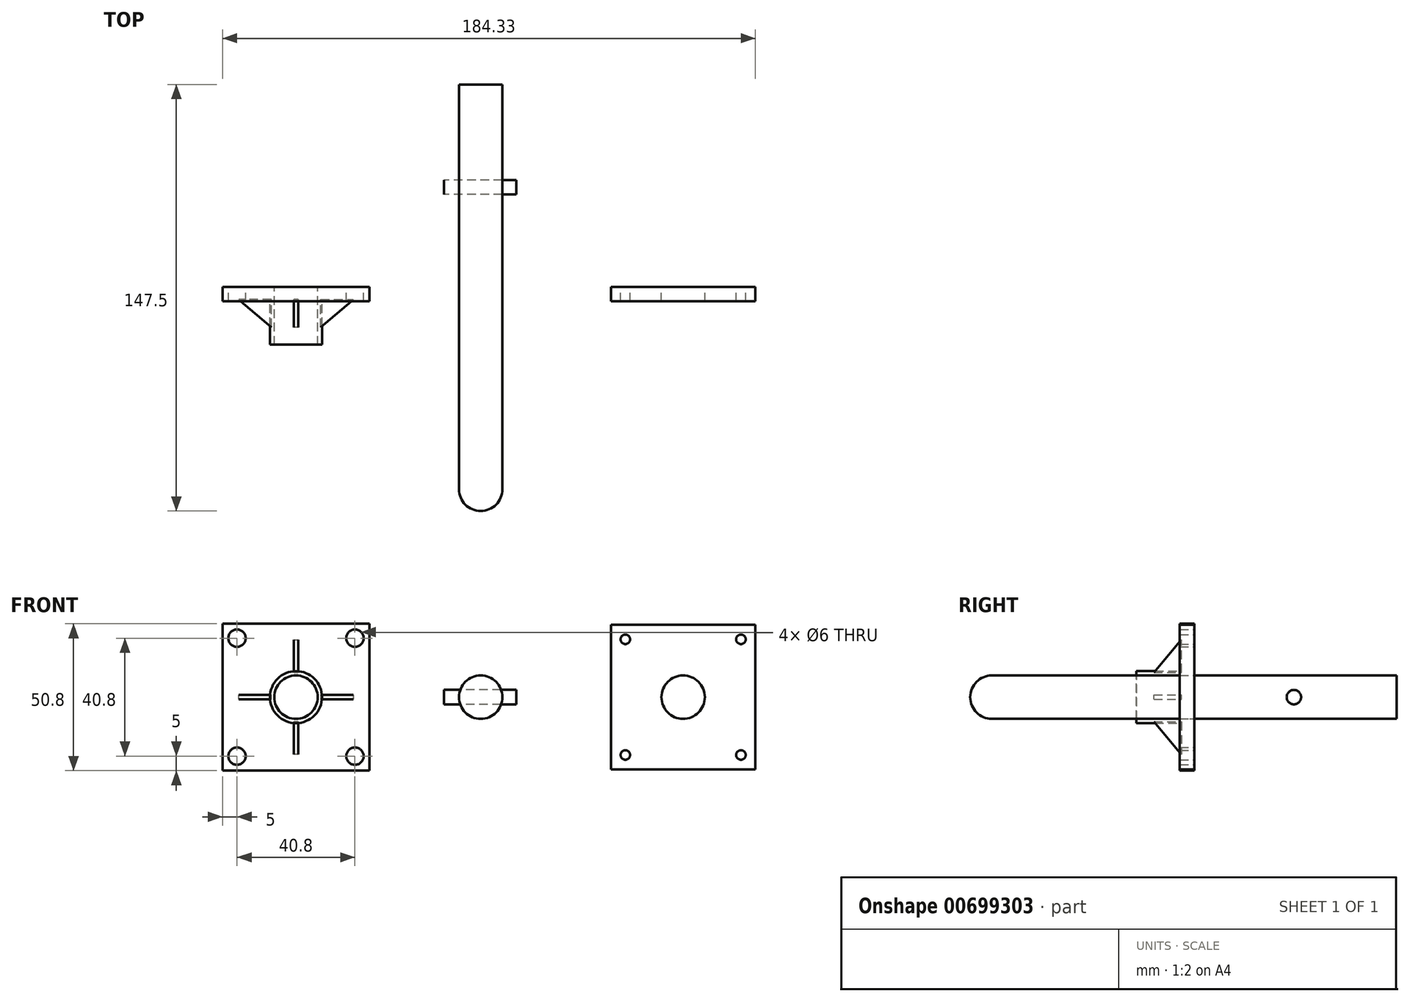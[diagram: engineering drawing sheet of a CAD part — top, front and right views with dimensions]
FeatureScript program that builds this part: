
annotation { "Feature Type Name" : "Feature", "Feature Type Description" : "" }
export const myFeature = defineFeature(function(context is Context, id is Id, definition is map)
    precondition{}
    {
        {
            var Q0;
            Q0=qCreatedBy(makeId("Front.planeOp"),FACE);
            var sketch = newSketch(context, id + "F0", { "sketchPlane" : qUnion([Q0])});
            skLineSegment(sketch, "E0.bottom", {"start": v(-25.4, 25.4) * mm, "end": v(25.4, 25.4) * mm});
            skLineSegment(sketch, "E0.top", {"start": v(-25.4, -25.4) * mm, "end": v(25.4, -25.4) * mm});
            skLineSegment(sketch, "E0.left", {"start": v(-25.4, 25.4) * mm, "end": v(-25.4, -25.4) * mm});
            skLineSegment(sketch, "E0.right", {"start": v(25.4, 25.4) * mm, "end": v(25.4, -25.4) * mm});
            skLineSegment(sketch, "E1", {"start": v(-20.4, 20.4) * mm, "end": v(-20.4, -20.4) * mm, "construction": true});
            skLineSegment(sketch, "E2", {"start": v(22.07, 20.4) * mm, "end": v(-16.45, 20.4) * mm, "construction": true});
            skCircle(sketch, "E3", {"center": v(-20.4, 20.4) * mm, "radius": 3 * mm});
            skLineSegment(sketch, "E4", {"start": v(-20.4, -20.4) * mm, "end": v(20.4, -20.4) * mm, "construction": true});
            skCircle(sketch, "E5", {"center": v(-20.4, -20.4) * mm, "radius": 3 * mm});
            skLineSegment(sketch, "E6", {"start": v(20.4, -20.4) * mm, "end": v(20.4, 20.4) * mm, "construction": true});
            skCircle(sketch, "E7", {"center": v(20.4, 20.4) * mm, "radius": 3 * mm});
            skCircle(sketch, "E8", {"center": v(20.4, -20.4) * mm, "radius": 3 * mm});
            skLineSegment(sketch, "E9", {"start": v(0, 25.4) * mm, "end": v(0, -20.4) * mm, "construction": true});
            skLineSegment(sketch, "E10", {"start": v(-20.4, 0) * mm, "end": v(20.4, 0) * mm, "construction": true});
            skCircle(sketch, "E11", {"center": v(0, 0) * mm, "radius": 7.5 * mm});
            skSolve(sketch);
        }
        {
            var Q0;
            Q0=makeQuery(id+"F0.imprint","IMPRINT",FACE,{"disambiguationData":[TD([[makeQuery(id+"F0.imprint","IMPRINT",EDGE,{"derivedFrom":sQuery(id+"F0.wireOp",EDGE,"E0.bottom")}),-1.0]])]});
            extrude(context, id + "F1", {"entities" : qUnion([Q0]), "depth" : 5 * mm, "offsetDistance" : 25 * mm});
        }
        {
            var Q0;
            Q0=makeQuery(id+"F1.opExtrude","CAP_FACE",FACE,{"disambiguationData":[OSD([sQuery(id+"F0.wireOp",EDGE,"E0.bottom"),sQuery(id+"F0.wireOp",EDGE,"E0.top"),sQuery(id+"F0.wireOp",EDGE,"E0.left"),sQuery(id+"F0.wireOp",EDGE,"E0.right"),sQuery(id+"F0.wireOp",EDGE,"E3"),sQuery(id+"F0.wireOp",EDGE,"E5"),sQuery(id+"F0.wireOp",EDGE,"E7"),sQuery(id+"F0.wireOp",EDGE,"E8"),sQuery(id+"F0.wireOp",EDGE,"E11")])],"isStart":false});
            var sketch = newSketch(context, id + "F2", { "sketchPlane" : qUnion([Q0])});
            skCircle(sketch, "E12", {"center": v(0, 0) * mm, "radius": 7.5 * mm});
            skCircle(sketch, "E13", {"center": v(0, 0) * mm, "radius": 9 * mm});
            skSolve(sketch);
        }
        {
            var Q0;
            Q0=makeQuery(id+"F2.imprint","IMPRINT",FACE,{"disambiguationData":[TD([[makeQuery(id+"F2.imprint","IMPRINT",EDGE,{"derivedFrom":sQuery(id+"F2.wireOp",EDGE,"E12")}),-1.0]])]});
            extrude(context, id + "F3", {"entities" : qUnion([Q0]), "operationType" : NewBodyOperationType.ADD, "depth" : 15 * mm, "offsetDistance" : 25 * mm});
        }
        {
            var Q0;
            Q0=qCreatedBy(makeId("Top.planeOp"),FACE);
            var sketch = newSketch(context, id + "F4", { "sketchPlane" : qUnion([Q0])});
            skLineSegment(sketch, "E14", {"start": v(8.55, -4.4) * mm, "end": v(19.84, -4.4) * mm});
            skLineSegment(sketch, "E15", {"start": v(19.84, -4.4) * mm, "end": v(8.55, -13.98) * mm});
            skLineSegment(sketch, "E16", {"start": v(8.55, -13.98) * mm, "end": v(8.55, -4.4) * mm});
            skSolve(sketch);
        }
        {
            var Q0;
            Q0=makeQuery(id+"F4.imprint","IMPRINT",FACE,{"disambiguationData":[TD([[makeQuery(id+"F4.imprint","IMPRINT",EDGE,{"derivedFrom":sQuery(id+"F4.wireOp",EDGE,"E14")}),-1.0]])]});
            extrude(context, id + "F5", {"entities" : qUnion([Q0]), "endBound" : BoundingType.SYMMETRIC, "depth" : 1.5 * mm, "offsetDistance" : 25 * mm});
        }
        {
            var Q0;
            Q0=makeQuery(id+"F5.opExtrude","SWEPT_BODY",BODY,{"disambiguationData":[OSD([sQuery(id+"F4.wireOp",EDGE,"E14"),sQuery(id+"F4.wireOp",EDGE,"E15"),sQuery(id+"F4.wireOp",EDGE,"E16")])]});
            var Q1;
            Q1=makeQuery(id+"F3.opExtrude","CAP_EDGE",EDGE,{"disambiguationData":[OSD([sQuery(id+"F2.wireOp",EDGE,"E12")])],"isStart":false});
            circularPattern(context, id + "F6", {"entities" : qUnion([Q0]), "axis" : qUnion([Q1]), "angle" : 360 * degree, "instanceCount" : 4, "equalSpace" : true});
        }
        {
            var Q0;
            Q0=qCreatedBy(makeId("Front.planeOp"),FACE);
            var sketch = newSketch(context, id + "F7", { "sketchPlane" : qUnion([Q0])});
            skCircle(sketch, "E17", {"center": v(63.9, 0) * mm, "radius": 7.5 * mm});
            skLineSegment(sketch, "E18", {"start": v(63.9, 0) * mm, "end": v(56.4, 0) * mm, "construction": true});
            skSolve(sketch);
        }
        {
            var Q0;
            Q0 = qSketchRegion(id + "F7", true);
            extrude(context, id + "F8", {"entities" : qUnion([Q0]), "endBound" : BoundingType.SYMMETRIC, "depth" : 140 * mm, "offsetDistance" : 25 * mm});
        }
        {
            var Q0;
            Q0=makeQuery(id+"F8.opExtrude","CAP_FACE",FACE,{"disambiguationData":[OSD([sQuery(id+"F7.wireOp",EDGE,"E17")])],"isStart":false});
            var sketch = newSketch(context, id + "F9", { "sketchPlane" : qUnion([Q0])});
            skLineSegment(sketch, "E19", {"start": v(44.74, 0) * mm, "end": v(63.9, 0) * mm, "construction": true});
            skArc(sketch, "E20", {"start": v(51.35, 0) * mm, "mid": v(63.9, 12.54) * mm, "end": v(76.44, 0) * mm});
            skLineSegment(sketch, "E21", {"start": v(51.35, 0) * mm, "end": v(76.44, 0) * mm});
            skSolve(sketch);
        }
        {
            var Q0;
            {var subQ0=sQuery(id+"F9.wireOp",EDGE,"E20");Q0=makeQuery(id+"F9.imprint","IMPRINT",FACE,{"disambiguationData":[TD([[makeQuery(id+"F9.imprint","IMPRINT",EDGE,{"derivedFrom":subQ0}),-1.0]])]});}
            var Q1;
            {var subQ0=sQuery(id+"F9.wireOp",EDGE,"E21");var subQ1=makeQuery(id+"F8.opExtrude","CAP_EDGE",EDGE,{"disambiguationData":[OSD([sQuery(id+"F7.wireOp",EDGE,"E17")])],"isStart":false});var subQ2=makeQuery(id+"F9.imprint","INTERSECT",VERTEX,{"disambiguationData":[OD(0.0)],"derivedFrom":[subQ1,subQ0]});Q1=makeQuery(id+"F9.imprint","IMPRINT",FACE,{"disambiguationData":[TD([[makeQuery(id+"F9.imprint","IMPRINT",EDGE,{"disambiguationData":[TD([[subQ2,-1.0]])],"derivedFrom":subQ0}),1.0]])]});}
            var Q2;
            Q2=sQuery(id+"F9.wireOp",EDGE,"E19");
            revolve(context, id + "F10", {"operationType" : NewBodyOperationType.ADD, "entities" : qUnion([Q0, Q1]), "axis" : qUnion([Q2]), "revolveType" : RevolveType.FULL});
        }
        {
            var Q0;
            Q0=qCreatedBy(makeId("Right.planeOp"),FACE);
            var sketch = newSketch(context, id + "F11", { "sketchPlane" : qUnion([Q0])});
            skCircle(sketch, "E22", {"center": v(34.48, 0) * mm, "radius": 2.5 * mm});
            skSolve(sketch);
        }
        {
            var Q0;
            Q0=makeQuery(id+"F11.imprint","IMPRINT",FACE,{"disambiguationData":[TD([[makeQuery(id+"F11.imprint","IMPRINT",EDGE,{"derivedFrom":sQuery(id+"F11.wireOp",EDGE,"E22")}),1.0]])]});
            extrude(context, id + "F12", {"entities" : qUnion([Q0]), "depth" : 25 * mm, "offsetDistance" : 25 * mm});
        }
        {
            var Q0;
            Q0=makeQuery(id+"F12.opExtrude","SWEPT_BODY",BODY,{"disambiguationData":[OSD([sQuery(id+"F11.wireOp",EDGE,"E22")])]});
            transform(context, id + "F13", {"entities" : qUnion([Q0]), "transformType" : TransformType.TRANSLATION_3D, "dx" : 51.2 * mm, "dy" : 0 * mm, "dz" : 0 * mm, "makeCopy" : false});
        }
        {
            var Q0;
            Q0=qCreatedBy(makeId("Front.planeOp"),FACE);
            var sketch = newSketch(context, id + "F14", { "sketchPlane" : qUnion([Q0])});
            skLineSegment(sketch, "E23.bottom", {"start": v(108.93, 25) * mm, "end": v(158.93, 25) * mm});
            skLineSegment(sketch, "E23.top", {"start": v(108.93, -25) * mm, "end": v(158.93, -25) * mm});
            skLineSegment(sketch, "E23.left", {"start": v(108.93, 25) * mm, "end": v(108.93, -25) * mm});
            skLineSegment(sketch, "E23.right", {"start": v(158.93, 25) * mm, "end": v(158.93, -25) * mm});
            skPoint(sketch, "E23.middle", {"position": v(133.93, 0) * mm});
            skLineSegment(sketch, "E24", {"start": v(108.93, 20) * mm, "end": v(158.93, 20) * mm, "construction": true});
            skLineSegment(sketch, "E25", {"start": v(153.93, 20) * mm, "end": v(153.93, -25) * mm, "construction": true});
            skLineSegment(sketch, "E26", {"start": v(113.93, 20) * mm, "end": v(113.93, -25) * mm, "construction": true});
            skLineSegment(sketch, "E27", {"start": v(113.93, -20) * mm, "end": v(153.93, -20) * mm, "construction": true});
            skCircle(sketch, "E28", {"center": v(113.93, 20) * mm, "radius": 1.65 * mm});
            skCircle(sketch, "E29", {"center": v(113.93, -20) * mm, "radius": 1.65 * mm});
            skCircle(sketch, "E30", {"center": v(153.93, 20) * mm, "radius": 1.65 * mm});
            skCircle(sketch, "E31", {"center": v(153.93, -20) * mm, "radius": 1.65 * mm});
            skCircle(sketch, "E32", {"center": v(133.93, 0) * mm, "radius": 7.5 * mm});
            skSolve(sketch);
        }
        {
            var Q0;
            Q0=makeQuery(id+"F14.imprint","IMPRINT",FACE,{"disambiguationData":[TD([[makeQuery(id+"F14.imprint","IMPRINT",EDGE,{"derivedFrom":sQuery(id+"F14.wireOp",EDGE,"E23.bottom")}),-1.0]])]});
            extrude(context, id + "F15", {"entities" : qUnion([Q0]), "depth" : 5 * mm, "offsetDistance" : 25 * mm});
        }
    });
